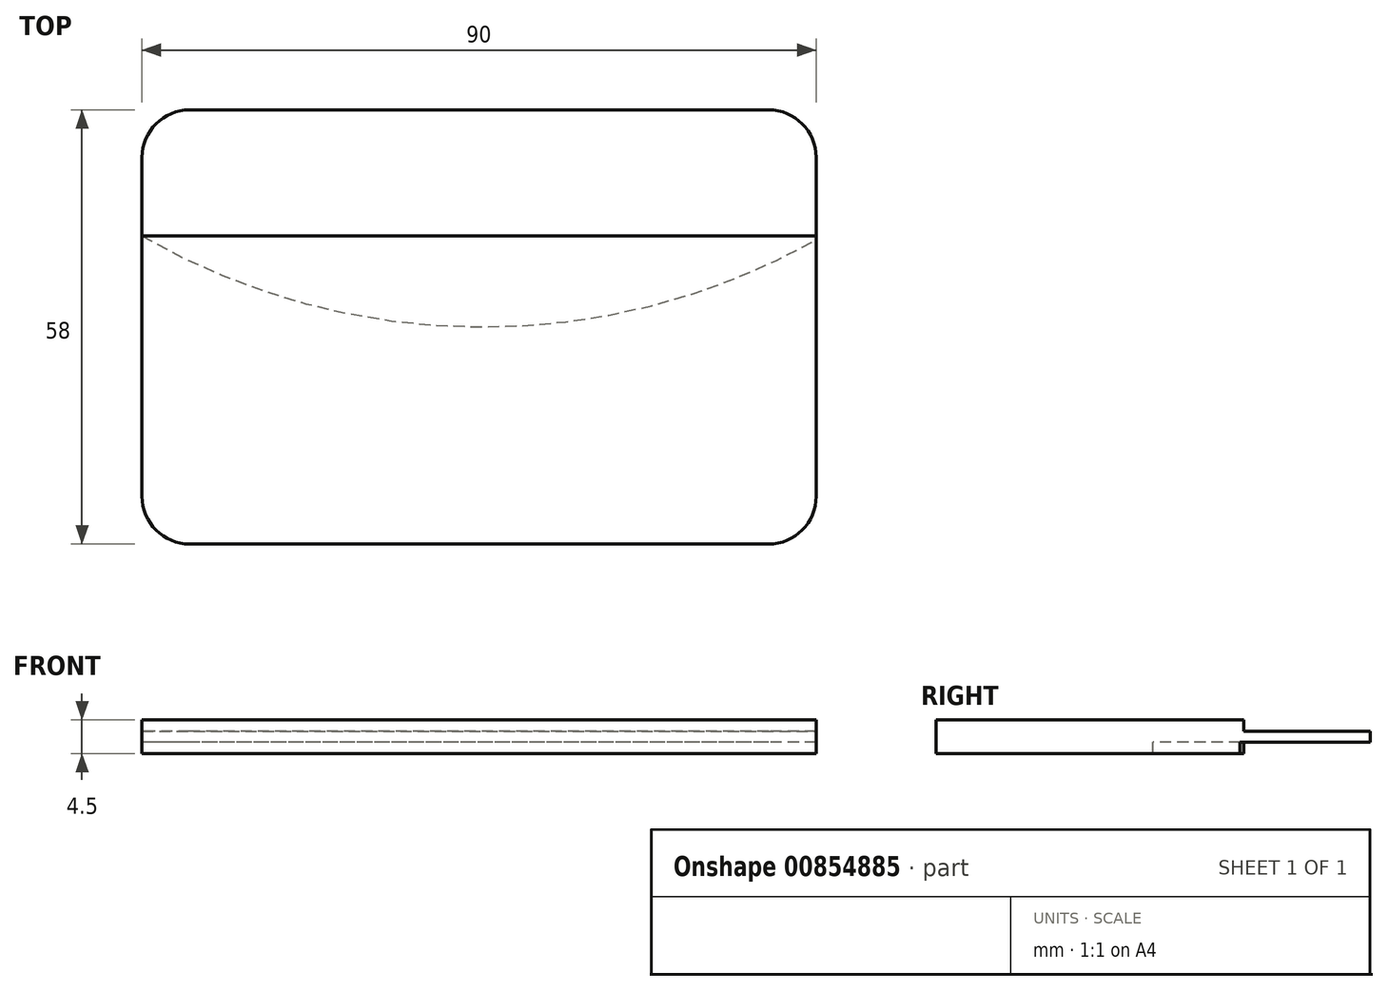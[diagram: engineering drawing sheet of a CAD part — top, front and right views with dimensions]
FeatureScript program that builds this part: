
annotation { "Feature Type Name" : "Feature", "Feature Type Description" : "" }
export const myFeature = defineFeature(function(context is Context, id is Id, definition is map)
    precondition{}
    {
        {
            var Q0;
            Q0=qCreatedBy(makeId("Top.planeOp"),FACE);
            var sketch = newSketch(context, id + "F0", { "sketchPlane" : qUnion([Q0])});
            skLineSegment(sketch, "E0.bottom", {"start": v(38.65, -29) * mm, "end": v(-38.65, -29) * mm});
            skLineSegment(sketch, "E0.top", {"start": v(38.65, 29) * mm, "end": v(-38.65, 29) * mm});
            skLineSegment(sketch, "E0.left", {"start": v(45, -22.65) * mm, "end": v(45, 22.65) * mm});
            skLineSegment(sketch, "E0.right", {"start": v(-45, -22.65) * mm, "end": v(-45, 22.65) * mm});
            skPoint(sketch, "E0.middle", {"position": v(0, 0) * mm});
            skPoint(sketch, "E1.visualSharp", {"position": v(-45, -29) * mm});
            skArc(sketch, "E1.filletArc", {"start": v(-45, -22.65) * mm, "mid": v(-43.14, -27.14) * mm, "end": v(-38.65, -29) * mm});
            skPoint(sketch, "E2.visualSharp", {"position": v(45, -29) * mm});
            skArc(sketch, "E2.filletArc", {"start": v(38.65, -29) * mm, "mid": v(43.14, -27.14) * mm, "end": v(45, -22.65) * mm});
            skPoint(sketch, "E3.visualSharp", {"position": v(-45, 29) * mm});
            skArc(sketch, "E3.filletArc", {"start": v(-38.65, 29) * mm, "mid": v(-43.14, 27.14) * mm, "end": v(-45, 22.65) * mm});
            skPoint(sketch, "E4.visualSharp", {"position": v(45, 29) * mm});
            skArc(sketch, "E4.filletArc", {"start": v(45, 22.65) * mm, "mid": v(43.14, 27.14) * mm, "end": v(38.65, 29) * mm});
            skSolve(sketch);
        }
        {
            var Q0;
            Q0=makeQuery(id+"F0.imprint","IMPRINT",FACE,{"disambiguationData":[TD([[makeQuery(id+"F0.imprint","IMPRINT",EDGE,{"derivedFrom":sQuery(id+"F0.wireOp",EDGE,"E0.bottom")}),-1.0]])]});
            extrude(context, id + "F1", {"entities" : qUnion([Q0]), "depth" : 1.5 * mm, "offsetDistance" : 25 * mm});
        }
        {
            var Q0;
            Q0=makeQuery(id+"F1.opExtrude","CAP_FACE",FACE,{"disambiguationData":[OSD([sQuery(id+"F0.wireOp",EDGE,"E0.bottom"),sQuery(id+"F0.wireOp",EDGE,"E0.top"),sQuery(id+"F0.wireOp",EDGE,"E0.left"),sQuery(id+"F0.wireOp",EDGE,"E0.right"),sQuery(id+"F0.wireOp",EDGE,"E1.filletArc"),sQuery(id+"F0.wireOp",EDGE,"E2.filletArc"),sQuery(id+"F0.wireOp",EDGE,"E3.filletArc"),sQuery(id+"F0.wireOp",EDGE,"E4.filletArc")])],"isStart":false});
            var sketch = newSketch(context, id + "F2", { "sketchPlane" : qUnion([Q0])});
            skLineSegment(sketch, "E5.0", {"start": v(45, -22.65) * mm, "end": v(45, 22.65) * mm});
            skLineSegment(sketch, "E6.0", {"start": v(-45, -22.65) * mm, "end": v(-45, 22.65) * mm});
            skArc(sketch, "E7.0", {"start": v(-45, -22.65) * mm, "mid": v(-43.14, -27.14) * mm, "end": v(-38.65, -29) * mm});
            skLineSegment(sketch, "E8.0", {"start": v(38.65, -29) * mm, "end": v(-38.65, -29) * mm});
            skArc(sketch, "E9.0", {"start": v(38.65, -29) * mm, "mid": v(43.14, -27.14) * mm, "end": v(45, -22.65) * mm});
            skLineSegment(sketch, "E10", {"start": v(-45, 12.13) * mm, "end": v(45, 12.13) * mm});
            skSolve(sketch);
        }
        {
            var Q0;
            {var subQ0=sQuery(id+"F2.wireOp",EDGE,"E7.0");Q0=makeQuery(id+"F2.imprint","IMPRINT",FACE,{"disambiguationData":[TD([[makeQuery(id+"F2.imprint","IMPRINT",EDGE,{"derivedFrom":subQ0}),1.0]])]});}
            extrude(context, id + "F3", {"entities" : qUnion([Q0]), "operationType" : NewBodyOperationType.ADD, "depth" : 1.5 * mm, "offsetDistance" : 25 * mm});
        }
        {
            var Q0;
            Q0=makeQuery(id+"F1.opExtrude","CAP_FACE",FACE,{"disambiguationData":[OSD([sQuery(id+"F0.wireOp",EDGE,"E0.bottom"),sQuery(id+"F0.wireOp",EDGE,"E0.top"),sQuery(id+"F0.wireOp",EDGE,"E0.left"),sQuery(id+"F0.wireOp",EDGE,"E0.right"),sQuery(id+"F0.wireOp",EDGE,"E1.filletArc"),sQuery(id+"F0.wireOp",EDGE,"E2.filletArc"),sQuery(id+"F0.wireOp",EDGE,"E3.filletArc"),sQuery(id+"F0.wireOp",EDGE,"E4.filletArc")])],"isStart":true});
            var sketch = newSketch(context, id + "F4", { "sketchPlane" : qUnion([Q0])});
            skArc(sketch, "E11.0", {"start": v(45, -22.65) * mm, "mid": v(43.14, -27.14) * mm, "end": v(38.65, -29) * mm});
            skLineSegment(sketch, "E12.0", {"start": v(38.65, -29) * mm, "end": v(-38.65, -29) * mm});
            skArc(sketch, "E13.0", {"start": v(-38.65, -29) * mm, "mid": v(-43.14, -27.14) * mm, "end": v(-45, -22.65) * mm});
            skPoint(sketch, "E14.0", {"position": v(-45, -12.13) * mm});
            skLineSegment(sketch, "E15.0", {"start": v(45, 22.65) * mm, "end": v(45, -22.65) * mm});
            skLineSegment(sketch, "E16.0", {"start": v(-45, 22.65) * mm, "end": v(-45, -22.65) * mm});
            skPoint(sketch, "E17.0", {"position": v(-38.65, 29) * mm});
            skArc(sketch, "E18.0", {"start": v(-45, 22.65) * mm, "mid": v(-43.14, 27.14) * mm, "end": v(-38.65, 29) * mm});
            skLineSegment(sketch, "E19.0", {"start": v(38.65, 29) * mm, "end": v(-38.65, 29) * mm});
            skArc(sketch, "E20.0", {"start": v(38.65, 29) * mm, "mid": v(43.14, 27.14) * mm, "end": v(45, 22.65) * mm});
            skLineSegment(sketch, "E21", {"start": v(45, 18.14) * mm, "end": v(-45, 18.14) * mm, "construction": true});
            skLineSegment(sketch, "E22", {"start": v(45, -11.6) * mm, "end": v(-45, -12.13) * mm, "construction": true});
            skArc(sketch, "E23", {"start": v(45, -11.6) * mm, "mid": v(-0.07, 0) * mm, "end": v(-45, -12.13) * mm});
            skSolve(sketch);
        }
        {
            var Q0;
            {var subQ0=sQuery(id+"F4.wireOp",EDGE,"E18.0");Q0=makeQuery(id+"F4.imprint","IMPRINT",FACE,{"disambiguationData":[TD([[makeQuery(id+"F4.imprint","IMPRINT",EDGE,{"derivedFrom":subQ0}),-1.0]])]});}
            extrude(context, id + "F5", {"entities" : qUnion([Q0]), "operationType" : NewBodyOperationType.ADD, "depth" : 1.5 * mm, "offsetDistance" : 25 * mm});
        }
    });
